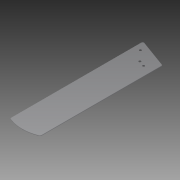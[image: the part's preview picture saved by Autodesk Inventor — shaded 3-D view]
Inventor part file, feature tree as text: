
AUTODESK INVENTOR PART (.ipt)
format: ipt  version: 2014 SP1 (Build 180222100, 222)  size: 136,704 bytes
history: native  units: in
note: dims shown in document units (in); Inventor stores cm internally (conversion verified against a paired STEP export)
features: sketch x3, extrude x2, fillet x2
ambient origin geometry x8: Origin, YZ Plane, XZ Plane, XY Plane, X Axis, Y Axis, Z Axis, Center Point
bodies: Solid1 (feature_tree)
feature tree (7):
  extrude  "Extrusion1"  Depth=0.0625in
  fillet  "Fillet1"  Radius=3.0937in
  fillet  "Fillet2"  Radius=0.0625in
  sketch  "Sketch3"  dims[d9=0.125in d10=0.025in]
  extrude  "Extrusion3"  Depth=0.025in
  sketch  "Sketch1"  dims[d3=10.0in d4=0.7559in d6=3.0937in d7=0.0625in d8=0.0in]
  sketch  "Sketch4"  dims[d24=0.165in d26=0.182in d27=0.5in d28=0.5in d29=1.1811in d31=0.5in d32=1.9685in d34=0.5in d37=1.0in d38=0.0in d39=0.1374in]
